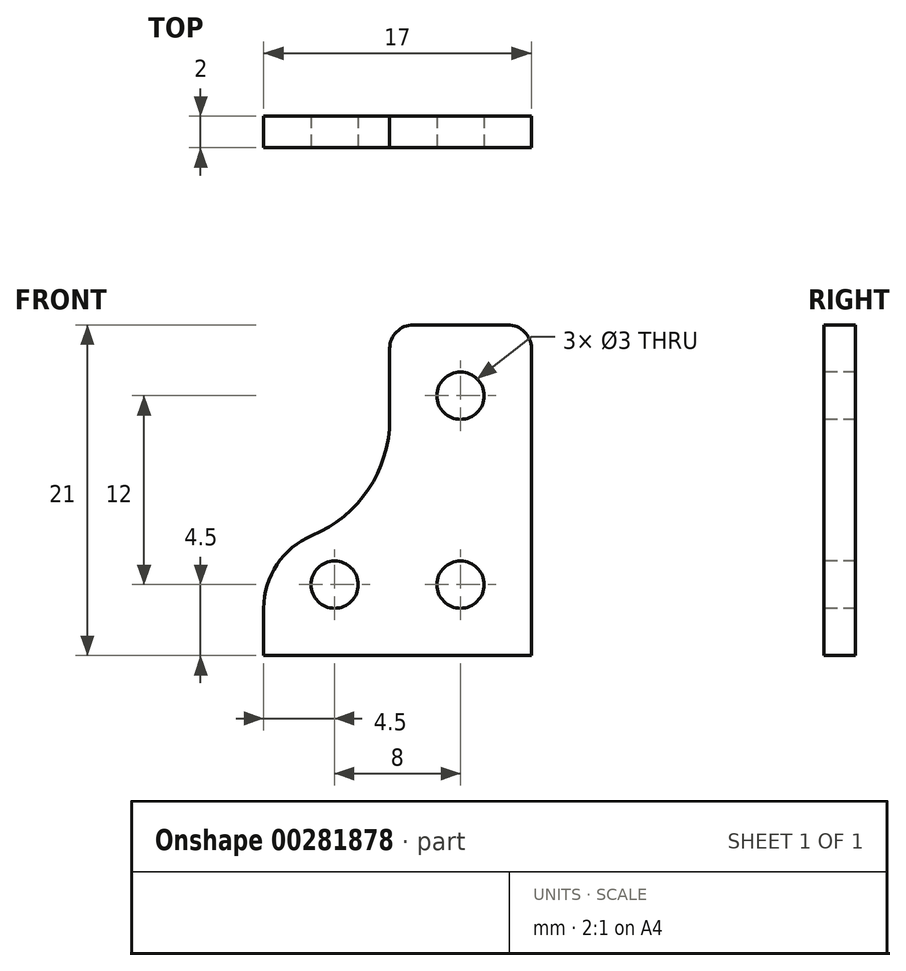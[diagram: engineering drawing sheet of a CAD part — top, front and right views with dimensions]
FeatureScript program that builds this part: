
annotation { "Feature Type Name" : "Feature", "Feature Type Description" : "" }
export const myFeature = defineFeature(function(context is Context, id is Id, definition is map)
    precondition{}
    {
        {
            var Q0;
            Q0=qCreatedBy(makeId("Front.planeOp"),FACE);
            var sketch = newSketch(context, id + "F0", { "sketchPlane" : qUnion([Q0])});
            skLineSegment(sketch, "E0.bottom", {"start": v(8.5, 7.5) * mm, "end": v(-8.5, 7.5) * mm});
            skLineSegment(sketch, "E0.top", {"start": v(8.5, -7.5) * mm, "end": v(-8.5, -7.5) * mm});
            skLineSegment(sketch, "E0.left", {"start": v(8.5, 7.5) * mm, "end": v(8.5, -7.5) * mm});
            skLineSegment(sketch, "E0.right", {"start": v(-8.5, 7.5) * mm, "end": v(-8.5, -7.5) * mm});
            skPoint(sketch, "E0.middle", {"position": v(0, 0) * mm});
            skSolve(sketch);
        }
        {
            var Q0;
            Q0=qSketchRegion(id+"F0",true);
            extrude(context, id + "F1", {"entities" : qUnion([Q0]), "depth" : 2 * mm});
        }
        {
            var Q0;
            Q0=makeQuery(id+"F1.opExtrude","CAP_FACE",FACE,{"disambiguationData":[OSD([sQuery(id+"F0.wireOp",EDGE,"E0.bottom"),sQuery(id+"F0.wireOp",EDGE,"E0.top"),sQuery(id+"F0.wireOp",EDGE,"E0.left"),sQuery(id+"F0.wireOp",EDGE,"E0.right")])],"isStart":false});
            var sketch = newSketch(context, id + "F2", { "sketchPlane" : qUnion([Q0])});
            skCircle(sketch, "E1", {"center": v(4, 3) * mm, "radius": 1.5 * mm, "construction": true});
            skCircle(sketch, "E2", {"center": v(-4, 3) * mm, "radius": 1.5 * mm, "construction": true});
            skCircle(sketch, "E3", {"center": v(-4, -3) * mm, "radius": 1.5 * mm});
            skCircle(sketch, "E4", {"center": v(4, -3) * mm, "radius": 1.5 * mm});
            skSolve(sketch);
        }
        {
            var Q0;
            Q0=qSketchRegion(id+"F2",true);
            extrude(context, id + "F3", {"entities" : qUnion([Q0]), "operationType" : NewBodyOperationType.REMOVE, "oppositeDirection" : true, "depth" : 25 * mm});
        }
        {
            var Q0;
            Q0=makeQuery(id+"F1.opExtrude","SWEPT_FACE",FACE,{"disambiguationData":[OSD([sQuery(id+"F0.wireOp",EDGE,"E0.bottom")])]});
            var sketch = newSketch(context, id + "F4", { "sketchPlane" : qUnion([Q0])});
            skLineSegment(sketch, "E5.bottom", {"start": v(8.5, 0) * mm, "end": v(-0.5, 0) * mm});
            skLineSegment(sketch, "E5.top", {"start": v(8.5, -2) * mm, "end": v(-0.5, -2) * mm});
            skLineSegment(sketch, "E5.left", {"start": v(8.5, 0) * mm, "end": v(8.5, -2) * mm});
            skLineSegment(sketch, "E5.right", {"start": v(-0.5, 0) * mm, "end": v(-0.5, -2) * mm});
            skSolve(sketch);
        }
        {
            var Q0;
            Q0=qSketchRegion(id+"F4",true);
            extrude(context, id + "F5", {"entities" : qUnion([Q0]), "operationType" : NewBodyOperationType.ADD, "depth" : 6 * mm});
        }
        {
            var Q0;
            Q0=makeQuery(id+"F5.boolean.opBoolean","MERGE",FACE,{"derivedFrom":[makeQuery(id+"F1.opExtrude","CAP_FACE",FACE,{"disambiguationData":[OSD([sQuery(id+"F0.wireOp",EDGE,"E0.bottom"),sQuery(id+"F0.wireOp",EDGE,"E0.top"),sQuery(id+"F0.wireOp",EDGE,"E0.left"),sQuery(id+"F0.wireOp",EDGE,"E0.right")])],"isStart":false}),makeQuery(id+"F5.opExtrude","SWEPT_FACE",FACE,{"disambiguationData":[OSD([sQuery(id+"F4.wireOp",EDGE,"E5.top")])]})]});
            var sketch = newSketch(context, id + "F6", { "sketchPlane" : qUnion([Q0])});
            skCircle(sketch, "E6", {"center": v(4, 9) * mm, "radius": 1.5 * mm});
            skSolve(sketch);
        }
        {
            var Q0;
            Q0=qSketchRegion(id+"F6",true);
            extrude(context, id + "F7", {"entities" : qUnion([Q0]), "operationType" : NewBodyOperationType.REMOVE, "oppositeDirection" : true, "depth" : 25 * mm});
        }
        {
            var Q0;
            Q0=makeQuery(id+"F5.opExtrude","CAP_EDGE",EDGE,{"disambiguationData":[OSD([sQuery(id+"F4.wireOp",EDGE,"E5.left")])],"isStart":false});
            var Q1;
            Q1=makeQuery(id+"F5.opExtrude","CAP_EDGE",EDGE,{"disambiguationData":[OSD([sQuery(id+"F4.wireOp",EDGE,"E5.right")])],"isStart":false});
            fillet(context, id + "F8", {"entities" : qUnion([Q0, Q1]), "radius" : 1.5 * mm, "tangentPropagation" : true, "allowEdgeOverflow" : false});
        }
        {
            var Q0;
            Q0=makeQuery(id+"F1.opExtrude","SWEPT_FACE",FACE,{"disambiguationData":[OSD([sQuery(id+"F0.wireOp",EDGE,"E0.top")])]});
            var sketch = newSketch(context, id + "F9", { "sketchPlane" : qUnion([Q0])});
            skLineSegment(sketch, "E7.bottom", {"start": v(-8.5, 2) * mm, "end": v(8.5, 2) * mm});
            skLineSegment(sketch, "E7.top", {"start": v(-8.5, 0) * mm, "end": v(8.5, 0) * mm});
            skLineSegment(sketch, "E7.left", {"start": v(-8.5, 2) * mm, "end": v(-8.5, 0) * mm});
            skLineSegment(sketch, "E7.right", {"start": v(8.5, 2) * mm, "end": v(8.5, 0) * mm});
            skSolve(sketch);
        }
        {
            var Q0;
            Q0=qSketchRegion(id+"F9",true);
            extrude(context, id + "F10", {"entities" : qUnion([Q0]), "operationType" : NewBodyOperationType.ADD, "depth" : 1 * mm});
        }
        {
            var Q0;
            Q0=makeQuery(id+"F10.opExtrude","CAP_FACE",FACE,{"disambiguationData":[OSD([sQuery(id+"F9.wireOp",EDGE,"E7.bottom"),sQuery(id+"F9.wireOp",EDGE,"E7.top"),sQuery(id+"F9.wireOp",EDGE,"E7.left"),sQuery(id+"F9.wireOp",EDGE,"E7.right")])],"isStart":false});
            var sketch = newSketch(context, id + "F11", { "sketchPlane" : qUnion([Q0])});
            skLineSegment(sketch, "E8.bottom", {"start": v(-8.5, 2) * mm, "end": v(8.5, 2) * mm});
            skLineSegment(sketch, "E8.top", {"start": v(-8.5, -4) * mm, "end": v(8.5, -4) * mm});
            skLineSegment(sketch, "E8.left", {"start": v(-8.5, 2) * mm, "end": v(-8.5, -4) * mm});
            skLineSegment(sketch, "E8.right", {"start": v(8.5, 2) * mm, "end": v(8.5, -4) * mm});
            skSolve(sketch);
        }
        {
            var Q0;
            Q0=qSketchRegion(id+"F11",true);
            extrude(context, id + "F12", {"entities" : qUnion([Q0]), "operationType" : NewBodyOperationType.ADD, "depth" : 8 * mm});
        }
        {
            var Q0;
            Q0=makeQuery(id+"F12.opExtrude","SWEPT_FACE",FACE,{"disambiguationData":[OSD([sQuery(id+"F11.wireOp",EDGE,"E8.top")])]});
            var sketch = newSketch(context, id + "F13", { "sketchPlane" : qUnion([Q0])});
            skLineSegment(sketch, "E9.bottom", {"start": v(-8.5, -8.5) * mm, "end": v(8.5, -8.5) * mm});
            skLineSegment(sketch, "E9.top", {"start": v(-8.5, -16.5) * mm, "end": v(8.5, -16.5) * mm});
            skLineSegment(sketch, "E9.left", {"start": v(-8.5, -8.5) * mm, "end": v(-8.5, -16.5) * mm});
            skLineSegment(sketch, "E9.right", {"start": v(8.5, -8.5) * mm, "end": v(8.5, -16.5) * mm});
            skSolve(sketch);
        }
        {
            var Q0;
            Q0=qSketchRegion(id+"F13",true);
            extrude(context, id + "F14", {"entities" : qUnion([Q0]), "operationType" : NewBodyOperationType.REMOVE, "oppositeDirection" : true, "depth" : 25 * mm});
        }
        {
            var Q0;
            Q0=makeQuery(id+"F14.boolean.opBoolean","COPY",FACE,{"derivedFrom":makeQuery(id+"F14.opExtrude","SWEPT_FACE",FACE,{"disambiguationData":[OSD([sQuery(id+"F13.wireOp",EDGE,"E9.bottom")])]})});
            var sketch = newSketch(context, id + "F15", { "sketchPlane" : qUnion([Q0])});
            skLineSegment(sketch, "E10.bottom", {"start": v(-8.5, 2) * mm, "end": v(8.5, 2) * mm});
            skLineSegment(sketch, "E10.top", {"start": v(-8.5, 0) * mm, "end": v(8.5, 0) * mm});
            skLineSegment(sketch, "E10.left", {"start": v(-8.5, 2) * mm, "end": v(-8.5, 0) * mm});
            skLineSegment(sketch, "E10.right", {"start": v(8.5, 2) * mm, "end": v(8.5, 0) * mm});
            skSolve(sketch);
        }
        {
            var Q0;
            Q0=qSketchRegion(id+"F15",true);
            extrude(context, id + "F16", {"entities" : qUnion([Q0]), "operationType" : NewBodyOperationType.REMOVE, "oppositeDirection" : true, "depth" : 1 * mm});
        }
        {
            var Q0;
            Q0=makeQuery(id+"F10.boolean.opBoolean","MERGE",FACE,{"derivedFrom":[makeQuery(id+"F5.boolean.opBoolean","MERGE",FACE,{"derivedFrom":[makeQuery(id+"F1.opExtrude","CAP_FACE",FACE,{"disambiguationData":[OSD([sQuery(id+"F0.wireOp",EDGE,"E0.bottom"),sQuery(id+"F0.wireOp",EDGE,"E0.top"),sQuery(id+"F0.wireOp",EDGE,"E0.left"),sQuery(id+"F0.wireOp",EDGE,"E0.right")])],"isStart":true}),makeQuery(id+"F5.opExtrude","SWEPT_FACE",FACE,{"disambiguationData":[OSD([sQuery(id+"F4.wireOp",EDGE,"E5.bottom")])]})]}),makeQuery(id+"F10.opExtrude","SWEPT_FACE",FACE,{"disambiguationData":[OSD([sQuery(id+"F9.wireOp",EDGE,"E7.top")])]})]});
            var sketch = newSketch(context, id + "F17", { "sketchPlane" : qUnion([Q0])});
            skCircle(sketch, "E11", {"center": v(8.5, 7.5) * mm, "radius": 8 * mm});
            skSolve(sketch);
        }
        {
            var Q0;
            Q0=qSketchRegion(id+"F17",true);
            extrude(context, id + "F18", {"entities" : qUnion([Q0]), "operationType" : NewBodyOperationType.REMOVE, "oppositeDirection" : true, "depth" : 25 * mm});
        }
        {
            var Q0;
            Q0=makeQuery(id+"F18.boolean.opBoolean","INTERSECT",EDGE,{"derivedFrom":[makeQuery(id+"F12.boolean.opBoolean","MERGE",FACE,{"derivedFrom":[makeQuery(id+"F10.boolean.opBoolean","MERGE",FACE,{"derivedFrom":[makeQuery(id+"F1.opExtrude","SWEPT_FACE",FACE,{"disambiguationData":[OSD([sQuery(id+"F0.wireOp",EDGE,"E0.right")])]}),makeQuery(id+"F10.opExtrude","SWEPT_FACE",FACE,{"disambiguationData":[OSD([sQuery(id+"F9.wireOp",EDGE,"E7.left")])]})]}),makeQuery(id+"F12.opExtrude","SWEPT_FACE",FACE,{"disambiguationData":[OSD([sQuery(id+"F11.wireOp",EDGE,"E8.left")])]})]}),makeQuery(id+"F18.opExtrude","SWEPT_FACE",FACE,{"disambiguationData":[OSD([sQuery(id+"F17.wireOp",EDGE,"E11")])]})]});
            fillet(context, id + "F19", {"entities" : qUnion([Q0]), "radius" : 5 * mm, "tangentPropagation" : true, "allowEdgeOverflow" : false});
        }
    });
